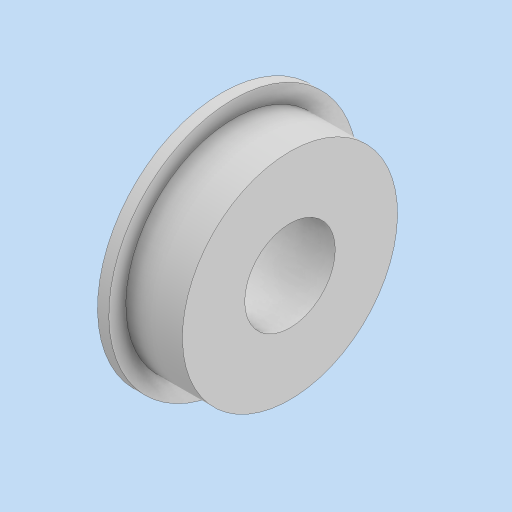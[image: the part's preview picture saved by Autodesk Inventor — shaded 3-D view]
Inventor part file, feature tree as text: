
AUTODESK INVENTOR PART (.ipt)
format: ipt  version: 2024 (Build 280153000, 153)  size: 130,560 bytes
history: native  units: in
note: dims shown in document units (in); Inventor stores cm internally (conversion verified against a paired STEP export)
features: extrude x2, sketch x2
ambient origin geometry x8: Origin, YZ Plane, XZ Plane, XY Plane, X Axis, Y Axis, Z Axis, Center Point
bodies: Solid1 (feature_tree)
feature tree (4):
  extrude  "Extrusion1"  Depth=0.315in
  extrude  "Extrusion2"  Depth=0.2362in
  sketch  "Sketch1"  dims[d0=0.8661in d1=0.315in]
  sketch  "Sketch2"  dims[d2=0.0394in d3=0.0in d4=0.748in d5=0.315in d6=0.2362in d7=0.0in]
